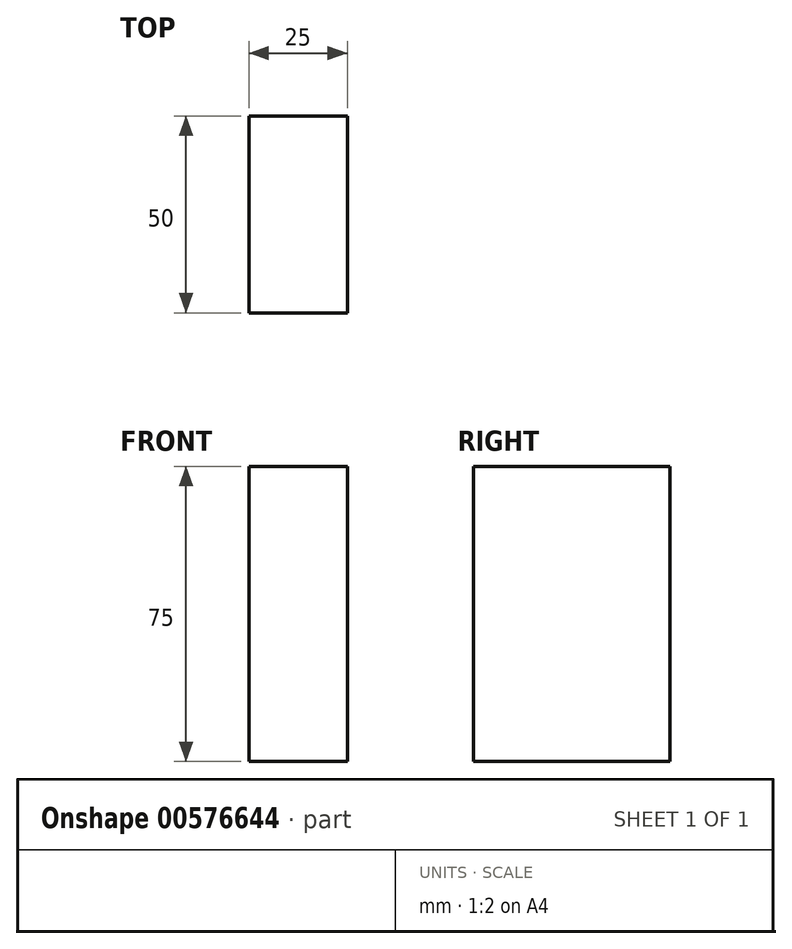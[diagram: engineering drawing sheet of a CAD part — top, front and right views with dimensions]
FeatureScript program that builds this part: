
annotation { "Feature Type Name" : "Feature", "Feature Type Description" : "" }
export const myFeature = defineFeature(function(context is Context, id is Id, definition is map)
    precondition{}
    {
        {
            var Q0;
            Q0=qCreatedBy(makeId("Top.planeOp"),FACE);
            var sketch = newSketch(context, id + "F0", { "sketchPlane" : qUnion([Q0])});
            skLineSegment(sketch, "E0.bottom", {"start": v(12.5, -25) * mm, "end": v(-12.5, -25) * mm});
            skLineSegment(sketch, "E0.top", {"start": v(12.5, 25) * mm, "end": v(-12.5, 25) * mm});
            skLineSegment(sketch, "E0.left", {"start": v(12.5, -25) * mm, "end": v(12.5, 25) * mm});
            skLineSegment(sketch, "E0.right", {"start": v(-12.5, -25) * mm, "end": v(-12.5, 25) * mm});
            skPoint(sketch, "E0.middle", {"position": v(0, 0) * mm});
            skSolve(sketch);
        }
        {
            var Q0;
            Q0=makeQuery(id+"F0.imprint","IMPRINT",FACE,{"disambiguationData":[TD([[makeQuery(id+"F0.imprint","IMPRINT",EDGE,{"derivedFrom":sQuery(id+"F0.wireOp",EDGE,"E0.bottom")}),-1.0]])]});
            extrude(context, id + "F1", {"entities" : qUnion([Q0]), "depth" : 75 * mm, "offsetDistance" : 25 * mm});
        }
    });
